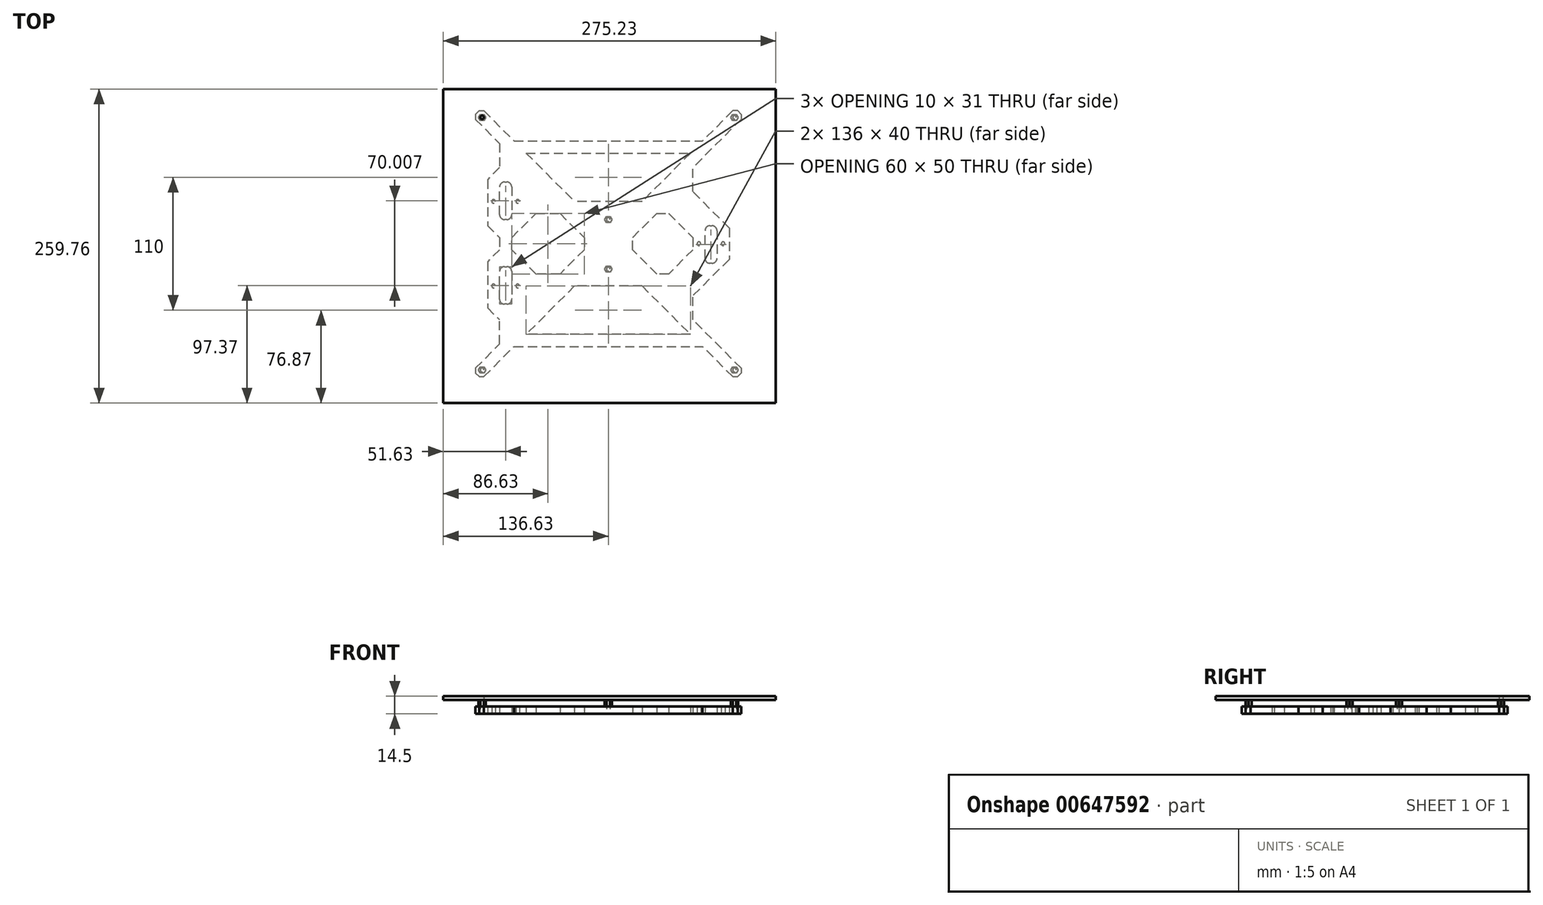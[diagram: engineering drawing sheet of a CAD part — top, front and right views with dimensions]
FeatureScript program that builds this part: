
annotation { "Feature Type Name" : "Feature", "Feature Type Description" : "" }
export const myFeature = defineFeature(function(context is Context, id is Id, definition is map)
    precondition{}
    {
        {
            var Q0;
            Q0=qCreatedBy(makeId("Top.planeOp"),FACE);
            var sketch = newSketch(context, id + "F0", { "sketchPlane" : qUnion([Q0])});
            skLineSegment(sketch, "E0", {"start": v(-120, 140) * mm, "end": v(-122, 140) * mm});
            skLineSegment(sketch, "E1", {"start": v(-122, 140) * mm, "end": v(-125, 137) * mm});
            skLineSegment(sketch, "E2", {"start": v(-125, 137) * mm, "end": v(-125, 135) * mm});
            skLineSegment(sketch, "E3", {"start": v(-125, 135) * mm, "end": v(-125, 133) * mm});
            skLineSegment(sketch, "E4", {"start": v(-125, 133) * mm, "end": v(-105, 113) * mm});
            skLineSegment(sketch, "E5", {"start": v(-105, 113) * mm, "end": v(-105, 93) * mm});
            skLineSegment(sketch, "E6", {"start": v(-105, 93) * mm, "end": v(-115, 83) * mm});
            skLineSegment(sketch, "E7", {"start": v(-115, -23) * mm, "end": v(-105, -33) * mm});
            skLineSegment(sketch, "E8", {"start": v(-125, -73) * mm, "end": v(-105, -53) * mm});
            skLineSegment(sketch, "E9", {"start": v(-105, -53) * mm, "end": v(-105, -33) * mm});
            skLineSegment(sketch, "E10", {"start": v(-125, -73) * mm, "end": v(-125, -77) * mm});
            skLineSegment(sketch, "E11", {"start": v(-125, -77) * mm, "end": v(-122, -80) * mm});
            skLineSegment(sketch, "E12", {"start": v(-122, -80) * mm, "end": v(-120, -80) * mm});
            skLineSegment(sketch, "E13", {"start": v(90, -80) * mm, "end": v(92, -80) * mm});
            skLineSegment(sketch, "E14", {"start": v(92, -80) * mm, "end": v(95, -77) * mm});
            skLineSegment(sketch, "E15", {"start": v(95, 136) * mm, "end": v(95, 137) * mm});
            skLineSegment(sketch, "E16", {"start": v(95, 137) * mm, "end": v(92, 140) * mm});
            skLineSegment(sketch, "E17", {"start": v(95, 133) * mm, "end": v(55, 93) * mm});
            skLineSegment(sketch, "E18", {"start": v(85, 43) * mm, "end": v(75, 53) * mm});
            skLineSegment(sketch, "E19", {"start": v(75, 53) * mm, "end": v(55, 73) * mm});
            skLineSegment(sketch, "E20", {"start": v(55, 73) * mm, "end": v(55, 93) * mm});
            skLineSegment(sketch, "E21", {"start": v(85, 17) * mm, "end": v(75, 7) * mm});
            skLineSegment(sketch, "E22", {"start": v(75, 7) * mm, "end": v(55, -13) * mm});
            skLineSegment(sketch, "E23", {"start": v(95, -73) * mm, "end": v(75, -53) * mm});
            skLineSegment(sketch, "E24", {"start": v(75, -53) * mm, "end": v(55, -33) * mm});
            skLineSegment(sketch, "E25", {"start": v(55, -33) * mm, "end": v(55, -13) * mm});
            skLineSegment(sketch, "E26", {"start": v(88, 140) * mm, "end": v(65, 117) * mm});
            skLineSegment(sketch, "E27", {"start": v(25, 77) * mm, "end": v(23, 75) * mm});
            skLineSegment(sketch, "E28", {"start": v(23, 75) * mm, "end": v(13, 65) * mm});
            skLineSegment(sketch, "E29", {"start": v(13, 65) * mm, "end": v(-43, 65) * mm});
            skLineSegment(sketch, "E30", {"start": v(88, -80) * mm, "end": v(63, -55) * mm});
            skLineSegment(sketch, "E31", {"start": v(13, -5) * mm, "end": v(-43, -5) * mm});
            skLineSegment(sketch, "E32", {"start": v(-93, 115) * mm, "end": v(63, 115) * mm});
            skLineSegment(sketch, "E33", {"start": v(-93, -55) * mm, "end": v(63, -55) * mm});
            skLineSegment(sketch, "E34", {"start": v(-115, 45) * mm, "end": v(-105, 35) * mm});
            skLineSegment(sketch, "E35", {"start": v(-105, 35) * mm, "end": v(-105, 25) * mm});
            skLineSegment(sketch, "E36", {"start": v(-105, 25) * mm, "end": v(-115, 15) * mm});
            skLineSegment(sketch, "E37", {"start": v(-95, 35) * mm, "end": v(-75, 55) * mm});
            skLineSegment(sketch, "E38", {"start": v(-75, 55) * mm, "end": v(-55, 55) * mm});
            skLineSegment(sketch, "E39", {"start": v(-55, 55) * mm, "end": v(-35, 35) * mm});
            skLineSegment(sketch, "E40", {"start": v(-35, 35) * mm, "end": v(-35, 25) * mm});
            skLineSegment(sketch, "E41", {"start": v(-35, 25) * mm, "end": v(-55, 5) * mm});
            skLineSegment(sketch, "E42", {"start": v(-55, 5) * mm, "end": v(-75, 5) * mm});
            skLineSegment(sketch, "E43", {"start": v(-75, 5) * mm, "end": v(-95, 25) * mm});
            skLineSegment(sketch, "E44", {"start": v(-95, 25) * mm, "end": v(-95, 35) * mm});
            skLineSegment(sketch, "E45", {"start": v(35, 55) * mm, "end": v(55, 35) * mm});
            skLineSegment(sketch, "E46", {"start": v(55, 35) * mm, "end": v(55, 25) * mm});
            skLineSegment(sketch, "E47", {"start": v(55, 25) * mm, "end": v(35, 5) * mm});
            skLineSegment(sketch, "E48", {"start": v(35, 5) * mm, "end": v(25, 5) * mm});
            skLineSegment(sketch, "E49", {"start": v(25, 5) * mm, "end": v(5, 25) * mm});
            skLineSegment(sketch, "E50", {"start": v(5, 25) * mm, "end": v(5, 35) * mm});
            skLineSegment(sketch, "E51", {"start": v(5, 35) * mm, "end": v(25, 55) * mm});
            skLineSegment(sketch, "E52", {"start": v(25, 55) * mm, "end": v(35, 55) * mm});
            skLineSegment(sketch, "E53", {"start": v(-120, 140) * mm, "end": v(-118, 140) * mm});
            skLineSegment(sketch, "E54", {"start": v(92, 140) * mm, "end": v(88, 140) * mm});
            skLineSegment(sketch, "E55", {"start": v(95, 136) * mm, "end": v(95, 133) * mm});
            skLineSegment(sketch, "E56", {"start": v(95, -73) * mm, "end": v(95, -77) * mm});
            skLineSegment(sketch, "E57", {"start": v(88, -80) * mm, "end": v(90, -80) * mm});
            skLineSegment(sketch, "E58", {"start": v(-118, -80) * mm, "end": v(-120, -80) * mm});
            skLineSegment(sketch, "E59", {"start": v(-83, 105) * mm, "end": v(53, 105) * mm});
            skLineSegment(sketch, "E60", {"start": v(65, 117) * mm, "end": v(63, 115) * mm});
            skLineSegment(sketch, "E61", {"start": v(53, 105) * mm, "end": v(25, 77) * mm});
            skLineSegment(sketch, "E62", {"start": v(-118, 140) * mm, "end": v(-93, 115) * mm});
            skLineSegment(sketch, "E63", {"start": v(-83, 105) * mm, "end": v(-43, 65) * mm});
            skLineSegment(sketch, "E64", {"start": v(53, -45) * mm, "end": v(-83, -45) * mm});
            skLineSegment(sketch, "E65", {"start": v(-118, -80) * mm, "end": v(-93, -55) * mm});
            skLineSegment(sketch, "E66", {"start": v(-43, -5) * mm, "end": v(-83, -45) * mm});
            skLineSegment(sketch, "E67", {"start": v(13, -5) * mm, "end": v(53, -45) * mm});
            skLineSegment(sketch, "E68", {"start": v(-115, 83) * mm, "end": v(-115, 45) * mm});
            skLineSegment(sketch, "E69", {"start": v(-115, 15) * mm, "end": v(-115, -23) * mm});
            skLineSegment(sketch, "E70", {"start": v(85, 43) * mm, "end": v(85, 17) * mm});
            skCircle(sketch, "E71", {"center": v(-110, 65) * mm, "radius": 1.5 * mm});
            skCircle(sketch, "E72", {"center": v(-90, 65) * mm, "radius": 1.5 * mm});
            skCircle(sketch, "E73", {"center": v(-110, -5) * mm, "radius": 1.5 * mm});
            skCircle(sketch, "E74", {"center": v(-90, -5) * mm, "radius": 1.5 * mm});
            skCircle(sketch, "E75", {"center": v(80, 30) * mm, "radius": 1.5 * mm});
            skCircle(sketch, "E76", {"center": v(60, 30) * mm, "radius": 1.5 * mm});
            skCircle(sketch, "E77", {"center": v(-119.5, 134.5) * mm, "radius": 1.5 * mm});
            skCircle(sketch, "E78", {"center": v(89.5, -74.5) * mm, "radius": 1.5 * mm});
            skCircle(sketch, "E79", {"center": v(89.5, 134.5) * mm, "radius": 1.5 * mm});
            skCircle(sketch, "E80", {"center": v(-119.5, -74.5) * mm, "radius": 1.5 * mm});
            skLineSegment(sketch, "E81", {"start": v(-105, -16) * mm, "end": v(-105, 7) * mm});
            skArc(sketch, "E82", {"start": v(-101, 11) * mm, "mid": v(-103.83, 9.83) * mm, "end": v(-105, 7) * mm});
            skLineSegment(sketch, "E83", {"start": v(-101, 11) * mm, "end": v(-99, 11) * mm});
            skArc(sketch, "E84", {"start": v(-95, 7) * mm, "mid": v(-96.17, 9.83) * mm, "end": v(-99, 11) * mm});
            skLineSegment(sketch, "E85", {"start": v(-95, 7) * mm, "end": v(-95, -16) * mm});
            skArc(sketch, "E86", {"start": v(-105, -16) * mm, "mid": v(-103.83, -18.83) * mm, "end": v(-101, -20) * mm});
            skLineSegment(sketch, "E87", {"start": v(-99, -20) * mm, "end": v(-101, -20) * mm});
            skArc(sketch, "E88", {"start": v(-99, -20) * mm, "mid": v(-96.17, -18.83) * mm, "end": v(-95, -16) * mm});
            skCircle(sketch, "E89", {"center": v(-15, 9) * mm, "radius": 1.5 * mm});
            skCircle(sketch, "E90", {"center": v(-15, 50) * mm, "radius": 1.5 * mm});
            skArc(sketch, "E91", {"start": v(-99, 50) * mm, "mid": v(-96.17, 51.18) * mm, "end": v(-95, 54) * mm});
            skLineSegment(sketch, "E92", {"start": v(-105, 54) * mm, "end": v(-105, 77) * mm});
            skArc(sketch, "E93", {"start": v(-101, 81) * mm, "mid": v(-103.83, 79.84) * mm, "end": v(-105, 77) * mm});
            skLineSegment(sketch, "E94", {"start": v(-101, 81) * mm, "end": v(-99, 81) * mm});
            skArc(sketch, "E95", {"start": v(-95, 77) * mm, "mid": v(-96.17, 79.84) * mm, "end": v(-99, 81) * mm});
            skLineSegment(sketch, "E96", {"start": v(-95, 77) * mm, "end": v(-95, 54) * mm});
            skArc(sketch, "E97", {"start": v(-105, 54) * mm, "mid": v(-103.83, 51.18) * mm, "end": v(-101, 50) * mm});
            skLineSegment(sketch, "E98", {"start": v(-99, 50) * mm, "end": v(-101, 50) * mm});
            skArc(sketch, "E99", {"start": v(71, 13.86) * mm, "mid": v(73.83, 15.03) * mm, "end": v(75, 17.86) * mm});
            skLineSegment(sketch, "E100", {"start": v(65, 17.86) * mm, "end": v(65, 40.86) * mm});
            skArc(sketch, "E101", {"start": v(69, 44.86) * mm, "mid": v(66.17, 43.7) * mm, "end": v(65, 40.86) * mm});
            skLineSegment(sketch, "E102", {"start": v(69, 44.86) * mm, "end": v(71, 44.86) * mm});
            skArc(sketch, "E103", {"start": v(75, 40.86) * mm, "mid": v(73.83, 43.7) * mm, "end": v(71, 44.86) * mm});
            skLineSegment(sketch, "E104", {"start": v(75, 40.86) * mm, "end": v(75, 17.86) * mm});
            skArc(sketch, "E105", {"start": v(65, 17.86) * mm, "mid": v(66.17, 15.03) * mm, "end": v(69, 13.86) * mm});
            skLineSegment(sketch, "E106", {"start": v(71, 13.86) * mm, "end": v(69, 13.86) * mm});
            skSolve(sketch);
        }
        {
            var Q0;
            Q0=makeQuery(id+"F0.imprint","IMPRINT",FACE,{"disambiguationData":[TD([[makeQuery(id+"F0.imprint","IMPRINT",EDGE,{"derivedFrom":sQuery(id+"F0.wireOp",EDGE,"E0")}),1.0]])]});
            extrude(context, id + "F1", {"entities" : qUnion([Q0]), "depth" : 6 * mm, "offsetDistance" : 25 * mm});
        }
        {
            var Q0;
            Q0=makeQuery(id+"F1.opExtrude","CAP_FACE",FACE,{"disambiguationData":[OSD([sQuery(id+"F0.wireOp",EDGE,"E0"),sQuery(id+"F0.wireOp",EDGE,"E1"),sQuery(id+"F0.wireOp",EDGE,"E2"),sQuery(id+"F0.wireOp",EDGE,"E3"),sQuery(id+"F0.wireOp",EDGE,"E4"),sQuery(id+"F0.wireOp",EDGE,"E5"),sQuery(id+"F0.wireOp",EDGE,"E6"),sQuery(id+"F0.wireOp",EDGE,"E7"),sQuery(id+"F0.wireOp",EDGE,"E8"),sQuery(id+"F0.wireOp",EDGE,"E9"),sQuery(id+"F0.wireOp",EDGE,"E10"),sQuery(id+"F0.wireOp",EDGE,"E11"),sQuery(id+"F0.wireOp",EDGE,"E12"),sQuery(id+"F0.wireOp",EDGE,"E13"),sQuery(id+"F0.wireOp",EDGE,"E14"),sQuery(id+"F0.wireOp",EDGE,"E15"),sQuery(id+"F0.wireOp",EDGE,"E16"),sQuery(id+"F0.wireOp",EDGE,"E17"),sQuery(id+"F0.wireOp",EDGE,"E18"),sQuery(id+"F0.wireOp",EDGE,"E19"),sQuery(id+"F0.wireOp",EDGE,"E20"),sQuery(id+"F0.wireOp",EDGE,"E21"),sQuery(id+"F0.wireOp",EDGE,"E22"),sQuery(id+"F0.wireOp",EDGE,"E23"),sQuery(id+"F0.wireOp",EDGE,"E24"),sQuery(id+"F0.wireOp",EDGE,"E25"),sQuery(id+"F0.wireOp",EDGE,"E26"),sQuery(id+"F0.wireOp",EDGE,"E27"),sQuery(id+"F0.wireOp",EDGE,"E28"),sQuery(id+"F0.wireOp",EDGE,"E29"),sQuery(id+"F0.wireOp",EDGE,"E30"),sQuery(id+"F0.wireOp",EDGE,"E31"),sQuery(id+"F0.wireOp",EDGE,"E32"),sQuery(id+"F0.wireOp",EDGE,"E33"),sQuery(id+"F0.wireOp",EDGE,"E34"),sQuery(id+"F0.wireOp",EDGE,"E35"),sQuery(id+"F0.wireOp",EDGE,"E36"),sQuery(id+"F0.wireOp",EDGE,"E37"),sQuery(id+"F0.wireOp",EDGE,"E38"),sQuery(id+"F0.wireOp",EDGE,"E39"),sQuery(id+"F0.wireOp",EDGE,"E40"),sQuery(id+"F0.wireOp",EDGE,"E41"),sQuery(id+"F0.wireOp",EDGE,"E42"),sQuery(id+"F0.wireOp",EDGE,"E43"),sQuery(id+"F0.wireOp",EDGE,"E44"),sQuery(id+"F0.wireOp",EDGE,"E45"),sQuery(id+"F0.wireOp",EDGE,"E46"),sQuery(id+"F0.wireOp",EDGE,"E47"),sQuery(id+"F0.wireOp",EDGE,"E48"),sQuery(id+"F0.wireOp",EDGE,"E49"),sQuery(id+"F0.wireOp",EDGE,"E50"),sQuery(id+"F0.wireOp",EDGE,"E51"),sQuery(id+"F0.wireOp",EDGE,"E52"),sQuery(id+"F0.wireOp",EDGE,"E53"),sQuery(id+"F0.wireOp",EDGE,"E54"),sQuery(id+"F0.wireOp",EDGE,"E55"),sQuery(id+"F0.wireOp",EDGE,"E56"),sQuery(id+"F0.wireOp",EDGE,"E57"),sQuery(id+"F0.wireOp",EDGE,"E58"),sQuery(id+"F0.wireOp",EDGE,"E59"),sQuery(id+"F0.wireOp",EDGE,"E60"),sQuery(id+"F0.wireOp",EDGE,"E61"),sQuery(id+"F0.wireOp",EDGE,"E62"),sQuery(id+"F0.wireOp",EDGE,"E63"),sQuery(id+"F0.wireOp",EDGE,"E64"),sQuery(id+"F0.wireOp",EDGE,"E65"),sQuery(id+"F0.wireOp",EDGE,"E66"),sQuery(id+"F0.wireOp",EDGE,"E67"),sQuery(id+"F0.wireOp",EDGE,"E68"),sQuery(id+"F0.wireOp",EDGE,"E69"),sQuery(id+"F0.wireOp",EDGE,"E70"),sQuery(id+"F0.wireOp",EDGE,"E71"),sQuery(id+"F0.wireOp",EDGE,"E72"),sQuery(id+"F0.wireOp",EDGE,"E73"),sQuery(id+"F0.wireOp",EDGE,"E74"),sQuery(id+"F0.wireOp",EDGE,"E75"),sQuery(id+"F0.wireOp",EDGE,"E76"),sQuery(id+"F0.wireOp",EDGE,"E77"),sQuery(id+"F0.wireOp",EDGE,"E78"),sQuery(id+"F0.wireOp",EDGE,"E79"),sQuery(id+"F0.wireOp",EDGE,"E80"),sQuery(id+"F0.wireOp",EDGE,"E81"),sQuery(id+"F0.wireOp",EDGE,"E82"),sQuery(id+"F0.wireOp",EDGE,"E83"),sQuery(id+"F0.wireOp",EDGE,"E84"),sQuery(id+"F0.wireOp",EDGE,"E85"),sQuery(id+"F0.wireOp",EDGE,"E86"),sQuery(id+"F0.wireOp",EDGE,"E87"),sQuery(id+"F0.wireOp",EDGE,"E88"),sQuery(id+"F0.wireOp",EDGE,"E89"),sQuery(id+"F0.wireOp",EDGE,"E90"),sQuery(id+"F0.wireOp",EDGE,"E91"),sQuery(id+"F0.wireOp",EDGE,"E92"),sQuery(id+"F0.wireOp",EDGE,"E93"),sQuery(id+"F0.wireOp",EDGE,"E94"),sQuery(id+"F0.wireOp",EDGE,"E95"),sQuery(id+"F0.wireOp",EDGE,"E96"),sQuery(id+"F0.wireOp",EDGE,"E97"),sQuery(id+"F0.wireOp",EDGE,"E98"),sQuery(id+"F0.wireOp",EDGE,"E99"),sQuery(id+"F0.wireOp",EDGE,"E100"),sQuery(id+"F0.wireOp",EDGE,"E101"),sQuery(id+"F0.wireOp",EDGE,"E102"),sQuery(id+"F0.wireOp",EDGE,"E103"),sQuery(id+"F0.wireOp",EDGE,"E104"),sQuery(id+"F0.wireOp",EDGE,"E105"),sQuery(id+"F0.wireOp",EDGE,"E106")])],"isStart":false});
            var sketch = newSketch(context, id + "F2", { "sketchPlane" : qUnion([Q0])});
            skCircle(sketch, "E107.cCircle", {"center": v(-119.5, 134.5) * mm, "radius": 3 * mm, "construction": true});
            skLineSegment(sketch, "E107.0", {"start": v(-116.5, 134.5) * mm, "end": v(-118, 131.9) * mm});
            skLineSegment(sketch, "E107.1", {"start": v(-118, 131.9) * mm, "end": v(-121, 131.9) * mm});
            skLineSegment(sketch, "E107.2", {"start": v(-121, 131.9) * mm, "end": v(-122.5, 134.5) * mm});
            skLineSegment(sketch, "E107.3", {"start": v(-122.5, 134.5) * mm, "end": v(-121, 137.1) * mm});
            skLineSegment(sketch, "E107.4", {"start": v(-121, 137.1) * mm, "end": v(-118, 137.1) * mm});
            skLineSegment(sketch, "E107.5", {"start": v(-118, 137.1) * mm, "end": v(-116.5, 134.5) * mm});
            skCircle(sketch, "E108.cCircle", {"center": v(89.5, 134.5) * mm, "radius": 3 * mm, "construction": true});
            skLineSegment(sketch, "E108.0", {"start": v(86.5, 134.5) * mm, "end": v(88, 137.1) * mm});
            skLineSegment(sketch, "E108.1", {"start": v(88, 137.1) * mm, "end": v(91, 137.1) * mm});
            skLineSegment(sketch, "E108.2", {"start": v(91, 137.1) * mm, "end": v(92.5, 134.5) * mm});
            skLineSegment(sketch, "E108.3", {"start": v(92.5, 134.5) * mm, "end": v(91, 131.9) * mm});
            skLineSegment(sketch, "E108.4", {"start": v(91, 131.9) * mm, "end": v(88, 131.9) * mm});
            skLineSegment(sketch, "E108.5", {"start": v(88, 131.9) * mm, "end": v(86.5, 134.5) * mm});
            skCircle(sketch, "E109.cCircle", {"center": v(89.5, -74.5) * mm, "radius": 3 * mm, "construction": true});
            skLineSegment(sketch, "E109.0", {"start": v(92.5, -74.5) * mm, "end": v(91, -77.1) * mm});
            skLineSegment(sketch, "E109.1", {"start": v(91, -77.1) * mm, "end": v(88, -77.1) * mm});
            skLineSegment(sketch, "E109.2", {"start": v(88, -77.1) * mm, "end": v(86.5, -74.5) * mm});
            skLineSegment(sketch, "E109.3", {"start": v(86.5, -74.5) * mm, "end": v(88, -71.9) * mm});
            skLineSegment(sketch, "E109.4", {"start": v(88, -71.9) * mm, "end": v(91, -71.9) * mm});
            skLineSegment(sketch, "E109.5", {"start": v(91, -71.9) * mm, "end": v(92.5, -74.5) * mm});
            skCircle(sketch, "E110.cCircle", {"center": v(-119.5, -74.5) * mm, "radius": 3 * mm, "construction": true});
            skLineSegment(sketch, "E110.0", {"start": v(-116.5, -74.5) * mm, "end": v(-118, -77.1) * mm});
            skLineSegment(sketch, "E110.1", {"start": v(-118, -77.1) * mm, "end": v(-121, -77.1) * mm});
            skLineSegment(sketch, "E110.2", {"start": v(-121, -77.1) * mm, "end": v(-122.5, -74.5) * mm});
            skLineSegment(sketch, "E110.3", {"start": v(-122.5, -74.5) * mm, "end": v(-121, -71.9) * mm});
            skLineSegment(sketch, "E110.4", {"start": v(-121, -71.9) * mm, "end": v(-118, -71.9) * mm});
            skLineSegment(sketch, "E110.5", {"start": v(-118, -71.9) * mm, "end": v(-116.5, -74.5) * mm});
            skCircle(sketch, "E111.cCircle", {"center": v(-15, 50) * mm, "radius": 3 * mm, "construction": true});
            skLineSegment(sketch, "E111.0", {"start": v(-12, 50) * mm, "end": v(-13.5, 47.4) * mm});
            skLineSegment(sketch, "E111.1", {"start": v(-13.5, 47.4) * mm, "end": v(-16.5, 47.4) * mm});
            skLineSegment(sketch, "E111.2", {"start": v(-16.5, 47.4) * mm, "end": v(-18, 50) * mm});
            skLineSegment(sketch, "E111.3", {"start": v(-18, 50) * mm, "end": v(-16.5, 52.6) * mm});
            skLineSegment(sketch, "E111.4", {"start": v(-16.5, 52.6) * mm, "end": v(-13.5, 52.6) * mm});
            skLineSegment(sketch, "E111.5", {"start": v(-13.5, 52.6) * mm, "end": v(-12, 50) * mm});
            skCircle(sketch, "E112.cCircle", {"center": v(-15, 9) * mm, "radius": 3 * mm, "construction": true});
            skLineSegment(sketch, "E112.0", {"start": v(-12, 9) * mm, "end": v(-13.5, 6.4) * mm});
            skLineSegment(sketch, "E112.1", {"start": v(-13.5, 6.4) * mm, "end": v(-16.5, 6.4) * mm});
            skLineSegment(sketch, "E112.2", {"start": v(-16.5, 6.4) * mm, "end": v(-18, 9) * mm});
            skLineSegment(sketch, "E112.3", {"start": v(-18, 9) * mm, "end": v(-16.5, 11.6) * mm});
            skLineSegment(sketch, "E112.4", {"start": v(-16.5, 11.6) * mm, "end": v(-13.5, 11.6) * mm});
            skLineSegment(sketch, "E112.5", {"start": v(-13.5, 11.6) * mm, "end": v(-12, 9) * mm});
            skSolve(sketch);
        }
        {
            var Q0;
            Q0=makeQuery(id+"F2.imprint","IMPRINT",FACE,{"disambiguationData":[TD([[makeQuery(id+"F2.imprint","IMPRINT",EDGE,{"derivedFrom":sQuery(id+"F2.wireOp",EDGE,"E107.0")}),-1.0]])]});
            extrude(context, id + "F3", {"entities" : qUnion([Q0]), "depth" : 5.3 * mm, "offsetDistance" : 25 * mm});
        }
        {
            var Q0;
            Q0=makeQuery(id+"F3.opExtrude","CAP_FACE",FACE,{"disambiguationData":[OSD([sQuery(id+"F0.wireOp",EDGE,"E77"),sQuery(id+"F2.wireOp",EDGE,"E107.0"),sQuery(id+"F2.wireOp",EDGE,"E107.1"),sQuery(id+"F2.wireOp",EDGE,"E107.2"),sQuery(id+"F2.wireOp",EDGE,"E107.3"),sQuery(id+"F2.wireOp",EDGE,"E107.4"),sQuery(id+"F2.wireOp",EDGE,"E107.5")])],"isStart":false});
            var sketch = newSketch(context, id + "F4", { "sketchPlane" : qUnion([Q0])});
            skLineSegment(sketch, "E113.bottom", {"start": v(-151.63, 157.9) * mm, "end": v(123.6, 157.9) * mm});
            skLineSegment(sketch, "E113.top", {"start": v(-151.63, -101.87) * mm, "end": v(123.6, -101.87) * mm});
            skLineSegment(sketch, "E113.left", {"start": v(-151.63, 157.9) * mm, "end": v(-151.63, -101.87) * mm});
            skLineSegment(sketch, "E113.right", {"start": v(123.6, 157.9) * mm, "end": v(123.6, -101.87) * mm});
            skSolve(sketch);
        }
        {
            var Q0;
            Q0=makeQuery(id+"F4.imprint","IMPRINT",FACE,{"disambiguationData":[TD([[makeQuery(id+"F4.imprint","IMPRINT",EDGE,{"derivedFrom":sQuery(id+"F4.wireOp",EDGE,"E113.bottom")}),-1.0]])]});
            var Q1;
            Q1=makeQuery(id+"F4.imprint","IMPRINT",FACE,{"disambiguationData":[TD([[makeQuery(id+"F4.imprint","IMPRINT",EDGE,{"derivedFrom":makeQuery(id+"F3.opExtrude","CAP_EDGE",EDGE,{"disambiguationData":[OSD([sQuery(id+"F2.wireOp",EDGE,"E107.0")])],"isStart":false})}),-1.0]])]});
            var Q2;
            Q2=makeQuery(id+"F4.imprint","IMPRINT",FACE,{"disambiguationData":[TD([[makeQuery(id+"F4.imprint","IMPRINT",EDGE,{"derivedFrom":makeQuery(id+"F3.opExtrude","CAP_EDGE",EDGE,{"disambiguationData":[OSD([sQuery(id+"F0.wireOp",EDGE,"E77")])],"isStart":false})}),-1.0]])]});
            extrude(context, id + "F5", {"entities" : qUnion([Q0, Q1, Q2]), "operationType" : NewBodyOperationType.ADD, "depth" : 3.2 * mm, "offsetDistance" : 25 * mm});
        }
        {
            var Q0;
            Q0=makeQuery(id+"F2.imprint","IMPRINT",FACE,{"disambiguationData":[TD([[makeQuery(id+"F2.imprint","IMPRINT",EDGE,{"derivedFrom":sQuery(id+"F2.wireOp",EDGE,"E110.0")}),-1.0]])]});
            var Q1;
            Q1=makeQuery(id+"F2.imprint","IMPRINT",FACE,{"disambiguationData":[TD([[makeQuery(id+"F2.imprint","IMPRINT",EDGE,{"derivedFrom":sQuery(id+"F2.wireOp",EDGE,"E112.0")}),-1.0]])]});
            var Q2;
            Q2=makeQuery(id+"F2.imprint","IMPRINT",FACE,{"disambiguationData":[TD([[makeQuery(id+"F2.imprint","IMPRINT",EDGE,{"derivedFrom":sQuery(id+"F2.wireOp",EDGE,"E111.0")}),-1.0]])]});
            var Q3;
            Q3=makeQuery(id+"F2.imprint","IMPRINT",FACE,{"disambiguationData":[TD([[makeQuery(id+"F2.imprint","IMPRINT",EDGE,{"derivedFrom":sQuery(id+"F2.wireOp",EDGE,"E108.0")}),-1.0]])]});
            var Q4;
            Q4=makeQuery(id+"F2.imprint","IMPRINT",FACE,{"disambiguationData":[TD([[makeQuery(id+"F2.imprint","IMPRINT",EDGE,{"derivedFrom":sQuery(id+"F2.wireOp",EDGE,"E109.0")}),-1.0]])]});
            var Q5;
            Q5=makeQuery(id+"F5.opExtrude","CAP_FACE",FACE,{"disambiguationData":[OSD([sQuery(id+"F0.wireOp",EDGE,"E77"),sQuery(id+"F4.wireOp",EDGE,"E113.bottom"),sQuery(id+"F4.wireOp",EDGE,"E113.top"),sQuery(id+"F4.wireOp",EDGE,"E113.left"),sQuery(id+"F4.wireOp",EDGE,"E113.right")])],"isStart":true});
            extrude(context, id + "F6", {"entities" : qUnion([Q0, Q1, Q2, Q3, Q4]), "operationType" : NewBodyOperationType.ADD, "endBound" : BoundingType.UP_TO_SURFACE, "depth" : 25 * mm, "endBoundEntityFace" : qUnion([Q5]), "offsetDistance" : 25 * mm});
        }
    });
